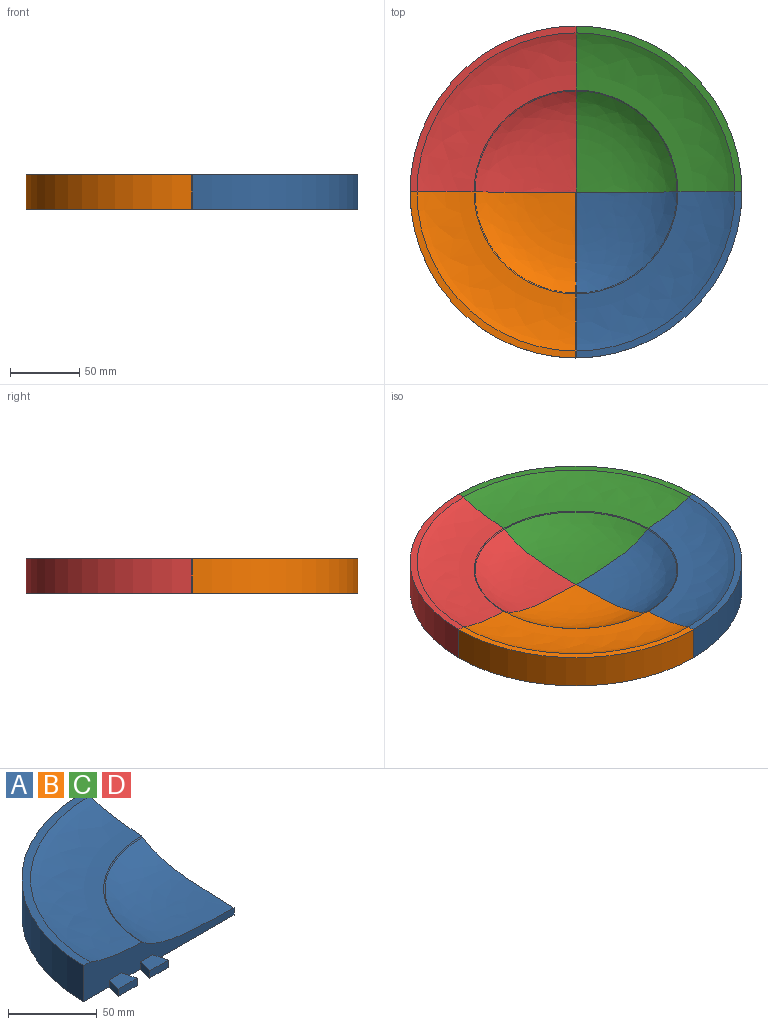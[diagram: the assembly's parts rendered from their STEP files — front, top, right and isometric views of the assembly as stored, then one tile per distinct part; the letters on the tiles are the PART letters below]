
ASSEMBLY  parts=4 mates=3
PART A: 31 faces, bbox 120x130x25 mm
  f0: plane 130x120mm, normal (0,0,-1), area 4871.2mm2, adj f2,f3,f8,f9,f10,f11,f13,f14
  f1: plane 120x120mm, normal (0,0,1), area 922.8mm2, adj f2,f3,f4,f8
  f2: plane 120x25mm, normal (0,-1,0), area 1454mm2, adj f0,f1,f3,f4,f5,f6,f7,f8
  f3: plane 120x25mm, normal (1,0,0), area 1448.9mm2, adj f0,f1,f2,f4,f5,f6,f7,f8
  f4: revolved ~115x115mm, area 6257.2mm2, adj f1,f2,f3,f5
  f5: revolved ~73.68x73.68mm, area 3.7mm2, adj f2,f3,f4,f6
  f6: revolved ~73.66x73.66mm, area 95.3mm2, adj f2,f3,f5,f7
  f7: revolved ~73x73mm, area 4397mm2, adj f2,f3,f6
  f8: cylinder r=120mm len=120mm, axis (0,0,1), area 4712.4mm2, adj f0,f1,f2,f3
  f9: plane 10x5mm, normal (0.97,0.24,0), area 51.5mm2, adj f0,f2,f10,f12
  f10: plane 15x5mm, normal (0,-1,0), area 75mm2, adj f0,f9,f11,f12
  f11: plane 10x5mm, normal (-0.97,0.24,0), area 51.5mm2, adj f0,f2,f10,f12
  f12: plane 15x10mm, normal (0,0,1), area 125.1mm2, adj f2,f9,f10,f11
  f13: plane 10x5mm, normal (0.97,0.24,0), area 51.5mm2, adj f0,f2,f14,f16
  f14: plane 15x5mm, normal (0,-1,0), area 75mm2, adj f0,f13,f15,f16
  f15: plane 10x5mm, normal (-0.97,0.24,0), area 51.5mm2, adj f0,f2,f14,f16
  f16: plane 15x10mm, normal (0,0,1), area 125.1mm2, adj f2,f13,f14,f15
  f17: plane 10x5.25mm, normal (-0.24,0.97,0), area 54.1mm2, adj f0,f3,f18,f20
  f18: plane 15x5.25mm, normal (1,0,0), area 78.8mm2, adj f0,f17,f19,f20
  f19: plane 10x5.25mm, normal (-0.24,-0.97,0), area 54.1mm2, adj f0,f3,f18,f20
  f20: plane 15x10mm, normal (0,0,-1), area 125.1mm2, adj f3,f17,f18,f19
  f21: plane 10x5.25mm, normal (-0.24,0.97,0), area 54.1mm2, adj f0,f3,f22,f24
  f22: plane 15x5.25mm, normal (1,0,0), area 78.8mm2, adj f0,f21,f23,f24
  f23: plane 10x5.25mm, normal (-0.24,-0.97,0), area 54.1mm2, adj f0,f3,f22,f24
  f24: plane 15x10mm, normal (0,0,-1), area 125.1mm2, adj f3,f21,f22,f23
  f25: plane 93.97x10mm, normal (0,1,0), area 411.8mm2, adj f0,f26,f27,f28,f29,f30
  f26: plane 93.97x10mm, normal (-1,0,0), area 411.8mm2, adj f0,f25,f27,f28,f29,f30
  f27: plane 65.99x65.99mm, normal (0,0,-1), area 3096.2mm2, adj f25,f26,f29
  f28: cylinder r=110mm len=93.97mm, axis (0,0,-1), area 1426.9mm2, adj f0,f25,f26,f30
  f29: cylinder r=82.37mm len=65.99mm, axis (0,0,-1), area 793.7mm2, adj f25,f26,f27,f30
  f30: plane 93.97x93.97mm, normal (0,0,-1), area 3342.4mm2, adj f25,f26,f28,f29
PART B: same geometry as A
PART C: same geometry as A
PART D: same geometry as A
PLACE A rot(axis=(0,0,1),180deg) t=(62.37,-60,0)mm
PLACE B rot(axis=(0,0,1),90deg) t=(-60,-62.37,0)mm
PLACE C rot(axis=(0,0,-1),90deg) t=(60,62.37,0)mm
PLACE D t=(-62.37,60,0)mm
MATE fastened C.f8 <-> D.f8  axis (0,0,-1) through (0,0,0)mm
MATE fastened B.f8 <-> D.f8  axis (0,0,-1) through (0,0,0)mm
MATE fastened A.f8 <-> C.f8  axis (0,0,-1) through (0,0,0)mm
